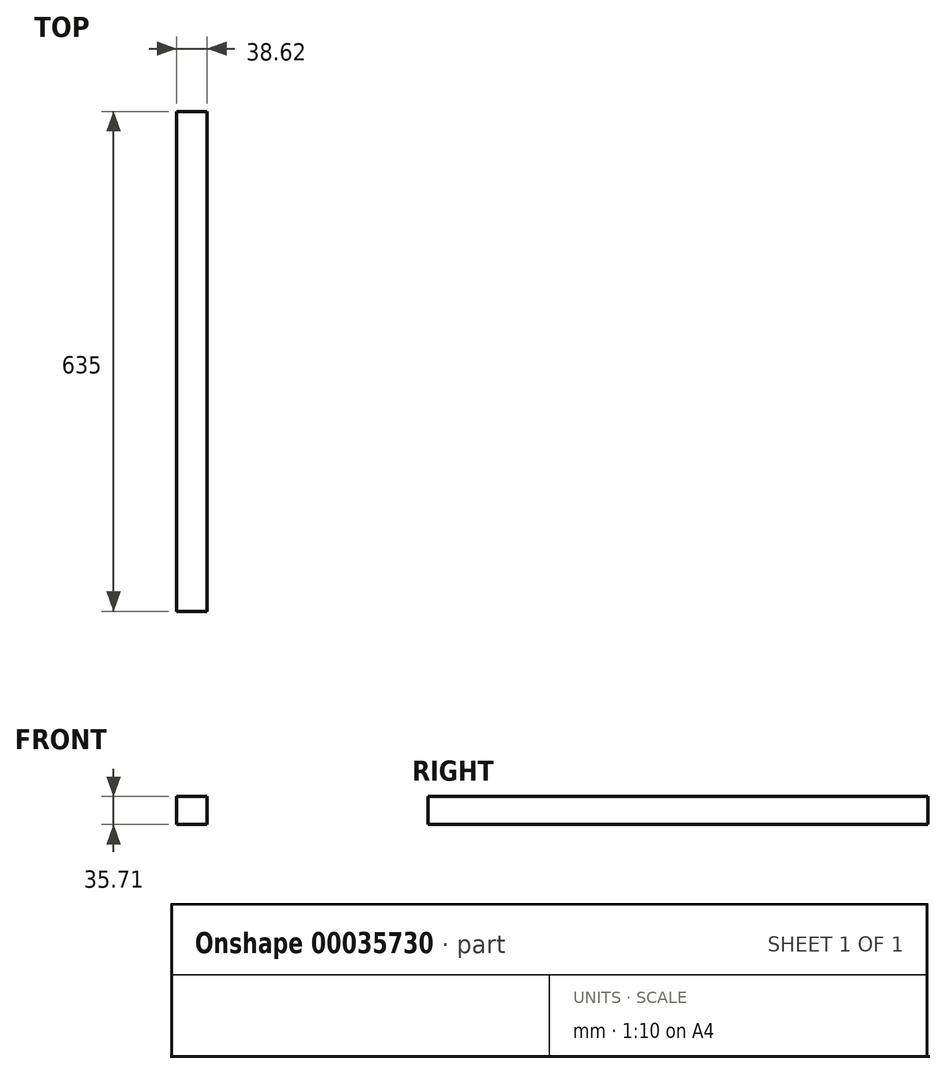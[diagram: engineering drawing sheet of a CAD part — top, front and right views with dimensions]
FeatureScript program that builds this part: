
annotation { "Feature Type Name" : "Feature", "Feature Type Description" : "" }
export const myFeature = defineFeature(function(context is Context, id is Id, definition is map)
    precondition{}
    {
        {
            var Q0;
            Q0=qCreatedBy(makeId("Front.planeOp"),FACE);
            var sketch = newSketch(context, id + "F0", { "sketchPlane" : qUnion([Q0])});
            skLineSegment(sketch, "E0", {"start": v(0, 0) * mm, "end": v(38.62, 0) * mm});
            skLineSegment(sketch, "E1", {"start": v(38.62, 0) * mm, "end": v(38.62, -35.7) * mm});
            skLineSegment(sketch, "E2", {"start": v(38.62, -35.7) * mm, "end": v(0, -35.7) * mm});
            skLineSegment(sketch, "E3", {"start": v(0, -35.7) * mm, "end": v(0, 0) * mm});
            skSolve(sketch);
        }
        {
            var Q0;
            Q0=makeQuery(id+"F0.imprint","IMPRINT",FACE,{"disambiguationData":[TD([[makeQuery(id+"F0.imprint","IMPRINT",EDGE,{"derivedFrom":sQuery(id+"F0.wireOp",EDGE,"E0")}),-1.0]])]});
            extrude(context, id + "F1", {"entities" : qUnion([Q0]), "depth" : 635 * mm});
        }
    });
